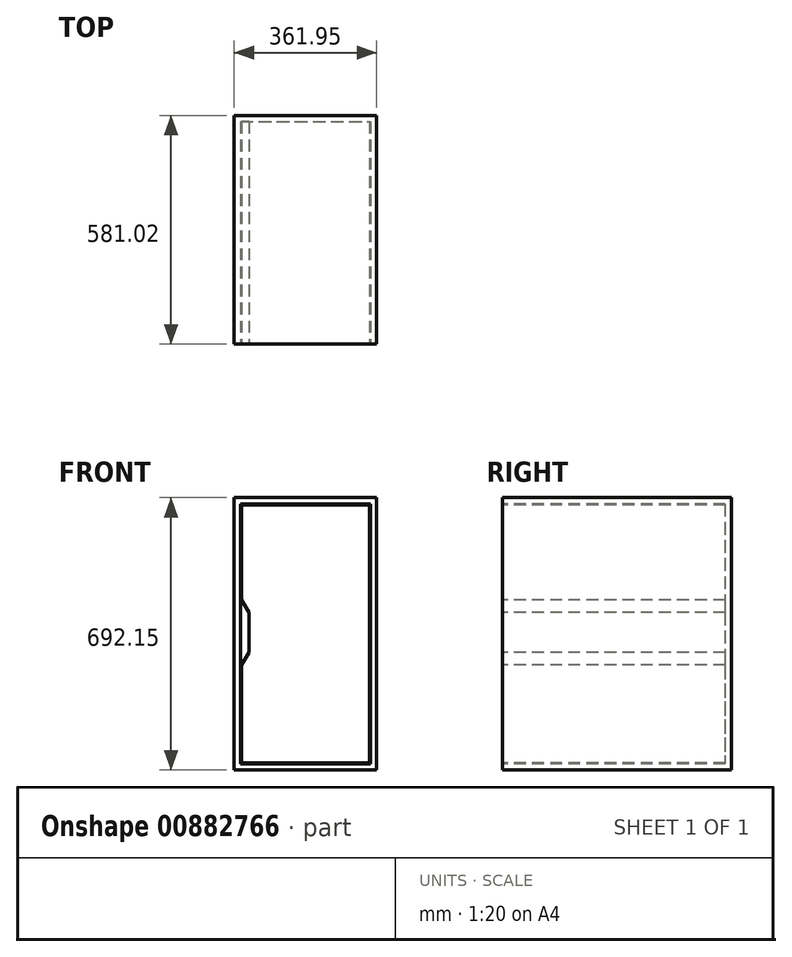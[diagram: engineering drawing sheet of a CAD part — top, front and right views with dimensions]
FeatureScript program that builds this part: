
annotation { "Feature Type Name" : "Feature", "Feature Type Description" : "" }
export const myFeature = defineFeature(function(context is Context, id is Id, definition is map)
    precondition{}
    {
        {
            var Q0;
            Q0=qCreatedBy(makeId("Front.planeOp"),FACE);
            var sketch = newSketch(context, id + "F0", { "sketchPlane" : qUnion([Q0])});
            skLineSegment(sketch, "E0.bottom", {"start": v(0, 0) * mm, "end": v(361.95, 0) * mm});
            skLineSegment(sketch, "E0.top", {"start": v(0, 692.15) * mm, "end": v(361.95, 692.15) * mm});
            skLineSegment(sketch, "E0.left", {"start": v(0, 0) * mm, "end": v(0, 692.15) * mm});
            skLineSegment(sketch, "E0.right", {"start": v(361.95, 0) * mm, "end": v(361.95, 692.15) * mm});
            skSolve(sketch);
        }
        {
            var Q0;
            Q0=qSketchRegion(id+"F0",true);
            extrude(context, id + "F1", {"entities" : qUnion([Q0]), "depth" : 581.02 * mm, "offsetDistance" : 25.4 * mm});
        }
        {
            var Q0;
            Q0=makeQuery(id+"F1.opExtrude","CAP_FACE",FACE,{"disambiguationData":[OSD([sQuery(id+"F0.wireOp",EDGE,"E0.bottom"),sQuery(id+"F0.wireOp",EDGE,"E0.top"),sQuery(id+"F0.wireOp",EDGE,"E0.left"),sQuery(id+"F0.wireOp",EDGE,"E0.right")])],"isStart":false});
            var sketch = newSketch(context, id + "F2", { "sketchPlane" : qUnion([Q0])});
            skLineSegment(sketch, "E1.bottom", {"start": v(15.87, 676.28) * mm, "end": v(346.08, 676.28) * mm});
            skLineSegment(sketch, "E1.top", {"start": v(15.88, 15.88) * mm, "end": v(346.08, 15.88) * mm});
            skLineSegment(sketch, "E1.left", {"start": v(15.87, 676.28) * mm, "end": v(15.88, 15.87) * mm});
            skLineSegment(sketch, "E1.right", {"start": v(346.08, 676.28) * mm, "end": v(346.08, 15.87) * mm});
            skSolve(sketch);
        }
        {
            var Q0;
            Q0=qSketchRegion(id+"F2",true);
            extrude(context, id + "F3", {"entities" : qUnion([Q0]), "operationType" : NewBodyOperationType.REMOVE, "oppositeDirection" : true, "depth" : 565.15 * mm, "offsetDistance" : 25.4 * mm});
        }
        {
            var Q0;
            Q0=makeQuery(id+"F1.opExtrude","CAP_FACE",FACE,{"disambiguationData":[OSD([sQuery(id+"F0.wireOp",EDGE,"E0.bottom"),sQuery(id+"F0.wireOp",EDGE,"E0.top"),sQuery(id+"F0.wireOp",EDGE,"E0.left"),sQuery(id+"F0.wireOp",EDGE,"E0.right")])],"isStart":false});
            var sketch = newSketch(context, id + "F4", { "sketchPlane" : qUnion([Q0])});
            skLineSegment(sketch, "E2.bottom", {"start": v(18.41, 673.74) * mm, "end": v(343.54, 673.74) * mm});
            skLineSegment(sketch, "E2.top", {"start": v(18.42, 18.42) * mm, "end": v(343.54, 18.42) * mm});
            skLineSegment(sketch, "E2.left", {"start": v(18.41, 673.74) * mm, "end": v(18.42, 18.42) * mm});
            skLineSegment(sketch, "E2.right", {"start": v(343.54, 673.74) * mm, "end": v(343.54, 18.42) * mm});
            skSolve(sketch);
        }
        {
            var Q0;
            Q0=makeQuery(id+"F4.imprint","IMPRINT",FACE,{"disambiguationData":[TD([[makeQuery(id+"F4.imprint","IMPRINT",EDGE,{"derivedFrom":sQuery(id+"F4.wireOp",EDGE,"E2.bottom")}),-1.0]])]});
            extrude(context, id + "F5", {"entities" : qUnion([Q0]), "operationType" : NewBodyOperationType.ADD, "oppositeDirection" : true, "depth" : 565.15 * mm, "offsetDistance" : 25.4 * mm});
        }
        {
            var Q0;
            Q0=makeQuery(id+"F5.opExtrude","CAP_FACE",FACE,{"disambiguationData":[OSD([sQuery(id+"F4.wireOp",EDGE,"E2.bottom"),sQuery(id+"F4.wireOp",EDGE,"E2.top"),sQuery(id+"F4.wireOp",EDGE,"E2.left"),sQuery(id+"F4.wireOp",EDGE,"E2.right")])],"isStart":true});
            var sketch = newSketch(context, id + "F6", { "sketchPlane" : qUnion([Q0])});
            skLineSegment(sketch, "E3", {"start": v(18.42, 431.8) * mm, "end": v(37.46, 400.05) * mm});
            skLineSegment(sketch, "E4", {"start": v(37.46, 400.05) * mm, "end": v(37.46, 298.45) * mm});
            skLineSegment(sketch, "E5", {"start": v(37.46, 298.45) * mm, "end": v(18.41, 266.7) * mm});
            skSolve(sketch);
        }
        {
            var Q0;
            {var subQ0=sQuery(id+"F6.wireOp",EDGE,"E3");Q0=makeQuery(id+"F6.imprint","IMPRINT",FACE,{"disambiguationData":[TD([[makeQuery(id+"F6.imprint","IMPRINT",EDGE,{"derivedFrom":subQ0}),-1.0]])]});}
            extrude(context, id + "F7", {"entities" : qUnion([Q0]), "operationType" : NewBodyOperationType.REMOVE, "oppositeDirection" : true, "depth" : 565.15 * mm, "offsetDistance" : 25.4 * mm});
        }
    });
